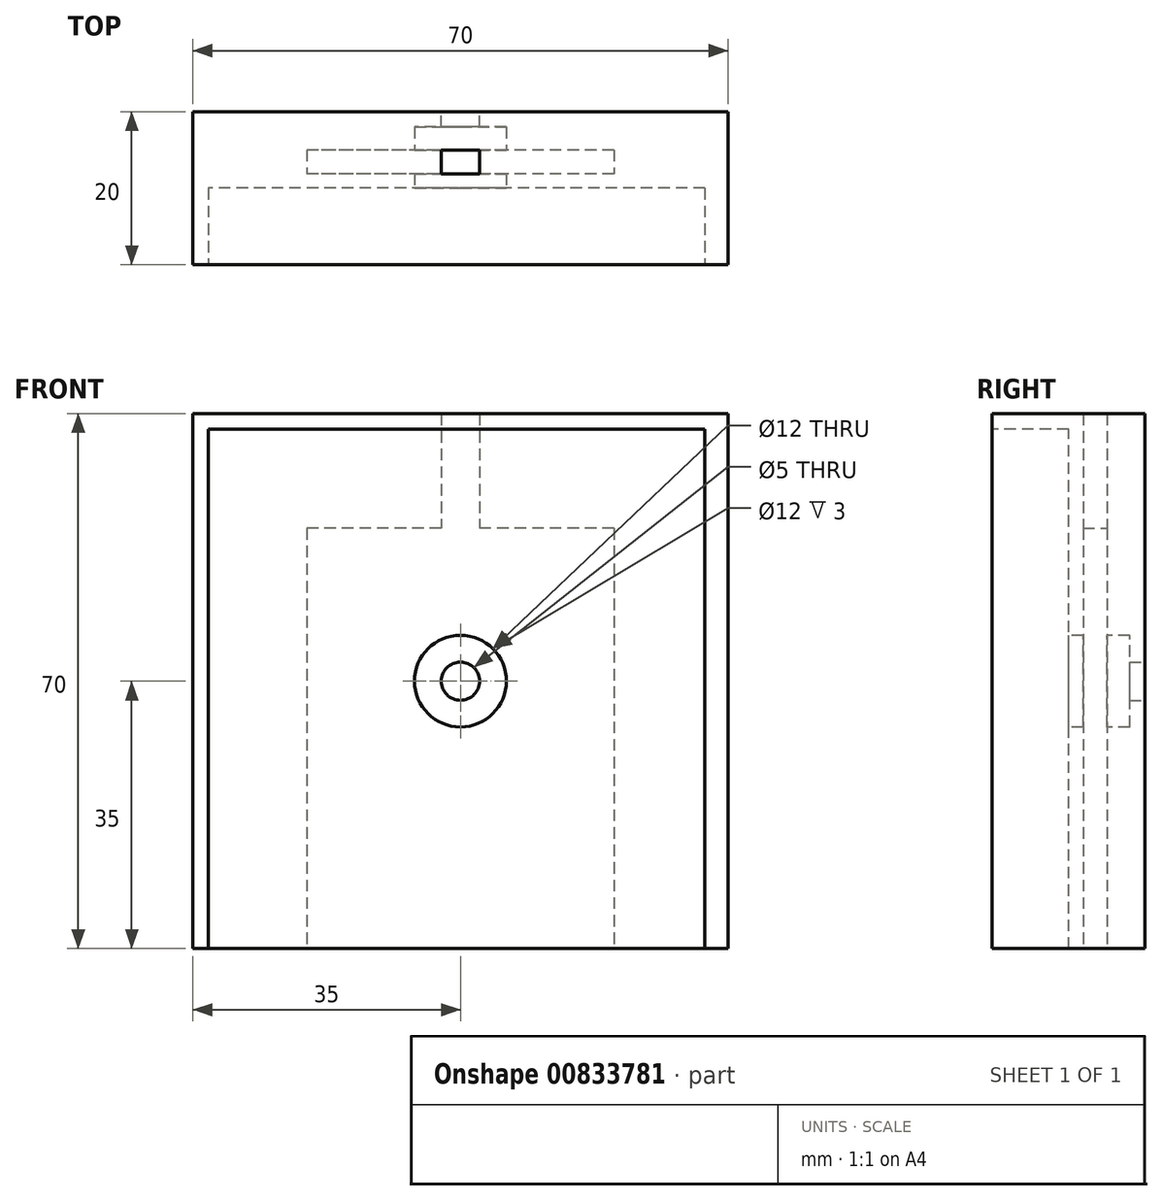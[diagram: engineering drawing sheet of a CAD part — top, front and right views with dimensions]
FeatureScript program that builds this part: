
annotation { "Feature Type Name" : "Feature", "Feature Type Description" : "" }
export const myFeature = defineFeature(function(context is Context, id is Id, definition is map)
    precondition{}
    {
        {
            var Q0;
            Q0=qCreatedBy(makeId("Front.planeOp"),FACE);
            var sketch = newSketch(context, id + "F0", { "sketchPlane" : qUnion([Q0])});
            skLineSegment(sketch, "E0.bottom", {"start": v(35, -35) * mm, "end": v(-35, -35) * mm});
            skLineSegment(sketch, "E0.top", {"start": v(35, 35) * mm, "end": v(-35, 35) * mm});
            skLineSegment(sketch, "E0.left", {"start": v(35, -35) * mm, "end": v(35, 35) * mm});
            skLineSegment(sketch, "E0.right", {"start": v(-35, -35) * mm, "end": v(-35, 35) * mm});
            skPoint(sketch, "E0.middle", {"position": v(0, 0) * mm});
            skCircle(sketch, "E1", {"center": v(0, 0) * mm, "radius": 2.5 * mm});
            skSolve(sketch);
        }
        {
            var Q0;
            Q0 = qSketchRegion(id + "F0", true);
            extrude(context, id + "F1", {"entities" : qUnion([Q0]), "depth" : 20 * mm, "offsetDistance" : 25 * mm});
        }
        {
            var Q0;
            Q0=makeQuery(id+"F1.opExtrude","SWEPT_FACE",FACE,{"disambiguationData":[OSD([sQuery(id+"F0.wireOp",EDGE,"E0.bottom")])]});
            var sketch = newSketch(context, id + "F2", { "sketchPlane" : qUnion([Q0])});
            skLineSegment(sketch, "E2.bottom", {"start": v(20.1, 5) * mm, "end": v(-20.1, 5) * mm});
            skLineSegment(sketch, "E2.top", {"start": v(20.1, 8.1) * mm, "end": v(-20.1, 8.1) * mm});
            skLineSegment(sketch, "E2.left", {"start": v(20.1, 5) * mm, "end": v(20.1, 8.1) * mm});
            skLineSegment(sketch, "E2.right", {"start": v(-20.1, 5) * mm, "end": v(-20.1, 8.1) * mm});
            skPoint(sketch, "E2.middle", {"position": v(0, 6.55) * mm});
            skSolve(sketch);
        }
        {
            var Q0;
            Q0 = qSketchRegion(id + "F2", true);
            extrude(context, id + "F3", {"entities" : qUnion([Q0]), "operationType" : NewBodyOperationType.REMOVE, "oppositeDirection" : true, "depth" : 55 * mm, "offsetDistance" : 25 * mm});
        }
        {
            var Q0;
            Q0=makeQuery(id+"F1.opExtrude","CAP_FACE",FACE,{"disambiguationData":[OSD([sQuery(id+"F0.wireOp",EDGE,"E0.bottom"),sQuery(id+"F0.wireOp",EDGE,"E0.top"),sQuery(id+"F0.wireOp",EDGE,"E0.left"),sQuery(id+"F0.wireOp",EDGE,"E0.right"),sQuery(id+"F0.wireOp",EDGE,"E1")])],"isStart":false});
            var sketch = newSketch(context, id + "F4", { "sketchPlane" : qUnion([Q0])});
            skCircle(sketch, "E3", {"center": v(0, 0) * mm, "radius": 6 * mm});
            skSolve(sketch);
        }
        {
            var Q0;
            Q0 = qSketchRegion(id + "F4", true);
            extrude(context, id + "F5", {"entities" : qUnion([Q0]), "operationType" : NewBodyOperationType.REMOVE, "oppositeDirection" : true, "depth" : 18 * mm, "offsetDistance" : 25 * mm});
        }
        {
            var Q0;
            Q0=makeQuery(id+"F1.opExtrude","CAP_FACE",FACE,{"disambiguationData":[OSD([sQuery(id+"F0.wireOp",EDGE,"E0.bottom"),sQuery(id+"F0.wireOp",EDGE,"E0.top"),sQuery(id+"F0.wireOp",EDGE,"E0.left"),sQuery(id+"F0.wireOp",EDGE,"E0.right"),sQuery(id+"F0.wireOp",EDGE,"E1")])],"isStart":false});
            var sketch = newSketch(context, id + "F6", { "sketchPlane" : qUnion([Q0])});
            skLineSegment(sketch, "E4.bottom", {"start": v(-33, -35) * mm, "end": v(32, -35) * mm});
            skLineSegment(sketch, "E4.top", {"start": v(-33, 33) * mm, "end": v(32, 33) * mm});
            skLineSegment(sketch, "E4.left", {"start": v(-33, -35) * mm, "end": v(-33, 33) * mm});
            skLineSegment(sketch, "E4.right", {"start": v(32, -35) * mm, "end": v(32, 33) * mm});
            skSolve(sketch);
        }
        {
            var Q0;
            Q0 = qSketchRegion(id + "F6", true);
            extrude(context, id + "F7", {"entities" : qUnion([Q0]), "operationType" : NewBodyOperationType.REMOVE, "oppositeDirection" : true, "depth" : 10 * mm, "offsetDistance" : 25 * mm});
        }
        {
            var Q0;
            Q0=makeQuery(id+"F3.boolean.opBoolean","COPY",FACE,{"derivedFrom":makeQuery(id+"F3.opExtrude","CAP_FACE",FACE,{"disambiguationData":[OSD([sQuery(id+"F2.wireOp",EDGE,"E2.bottom"),sQuery(id+"F2.wireOp",EDGE,"E2.top"),sQuery(id+"F2.wireOp",EDGE,"E2.left"),sQuery(id+"F2.wireOp",EDGE,"E2.right")])],"isStart":false})});
            var sketch = newSketch(context, id + "F8", { "sketchPlane" : qUnion([Q0])});
            skLineSegment(sketch, "E5.bottom", {"start": v(-2.5, 8.1) * mm, "end": v(2.5, 8.1) * mm});
            skLineSegment(sketch, "E5.top", {"start": v(-2.5, 5) * mm, "end": v(2.5, 5) * mm});
            skLineSegment(sketch, "E5.left", {"start": v(-2.5, 8.1) * mm, "end": v(-2.5, 5) * mm});
            skLineSegment(sketch, "E5.right", {"start": v(2.5, 8.1) * mm, "end": v(2.5, 5) * mm});
            skSolve(sketch);
        }
        {
            var Q0;
            Q0 = qSketchRegion(id + "F8", true);
            extrude(context, id + "F9", {"entities" : qUnion([Q0]), "operationType" : NewBodyOperationType.REMOVE, "endBound" : BoundingType.THROUGH_ALL, "oppositeDirection" : true, "depth" : 25 * mm, "offsetDistance" : 25 * mm});
        }
    });
